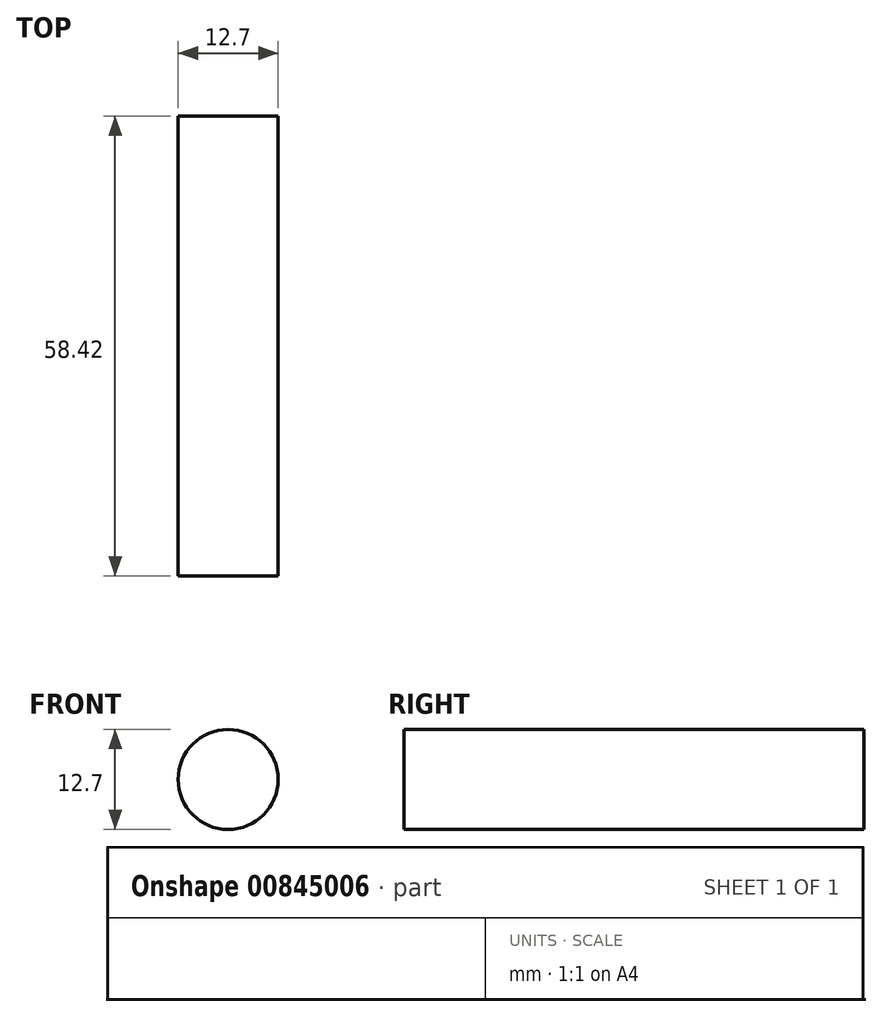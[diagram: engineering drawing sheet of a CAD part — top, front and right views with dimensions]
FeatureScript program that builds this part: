
annotation { "Feature Type Name" : "Feature", "Feature Type Description" : "" }
export const myFeature = defineFeature(function(context is Context, id is Id, definition is map)
    precondition{}
    {
        {
            var Q0;
            Q0=qCreatedBy(makeId("Front.planeOp"),FACE);
            var sketch = newSketch(context, id + "F0", { "sketchPlane" : qUnion([Q0])});
            skCircle(sketch, "E0", {"center": v(0, 0) * mm, "radius": 6.35 * mm});
            skSolve(sketch);
        }
        {
            var Q0;
            Q0 = qSketchRegion(id + "F0", true);
            extrude(context, id + "F1", {"entities" : qUnion([Q0]), "depth" : 29.2 * mm, "offsetDistance" : 25.4 * mm, "hasSecondDirection" : true, "secondDirectionOppositeDirection" : true, "secondDirectionDepth" : 29.2 * mm});
        }
    });
